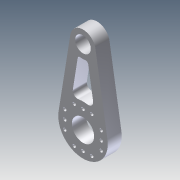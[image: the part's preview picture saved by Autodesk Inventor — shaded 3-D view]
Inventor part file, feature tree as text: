
AUTODESK INVENTOR PART (.ipt)
format: ipt  version: 2014 SP1 (Build 180222100, 222)  size: 221,184 bytes
history: native  units: in
note: dims shown in document units (in); Inventor stores cm internally (conversion verified against a paired STEP export)
features: extrude x5, sketch x5, fillet x2, other x1, move_body x1, imported_body x1
ambient origin geometry x8: Origin, YZ Plane, XZ Plane, XY Plane, X Axis, Y Axis, Z Axis, Center Point
bodies: Solid1 (feature_tree)
feature tree (15):
  other  "Component7.ipt1"
  move_body  "Move Body1"
  extrude  "Extrusion1"  Depth=0.25in
  extrude  "Extrusion2"  Depth=0.1969in TaperAngle=0.0deg
  extrude  "Extrusion3"  Depth=0.1969in TaperAngle=0.0deg
  extrude  "Extrusion4"  Depth=0.1575in
  extrude  "Extrusion5"  Depth=0.0787in
  fillet  "Fillet1"  Radius=0.0394in
  fillet  "Fillet2"  [1 undecoded]
  imported_body  "Base1"
  sketch  "Sketch1"  dims[d0=180.0deg d1=0.25in]
  sketch  "Sketch2"  dims[d2=0.4075in d3=0.1969in d4=0.0in]
  sketch  "Sketch3"  dims[d5=0.1969in d6=0.0in d10=0.1969in d11=0.0in]
  sketch  "Sketch4"  dims[d12=0.1969in d13=0.0in d14=0.1575in]
  sketch  "Sketch5"  dims[d15=0.1969in d16=0.0in d17=0.0787in d18=0.0394in]
note: 1 required parameter value undecoded (feature->parameter linkage not recoverable at this tier; creation-order binding heuristic only, values carry confidence <= 0.55)
